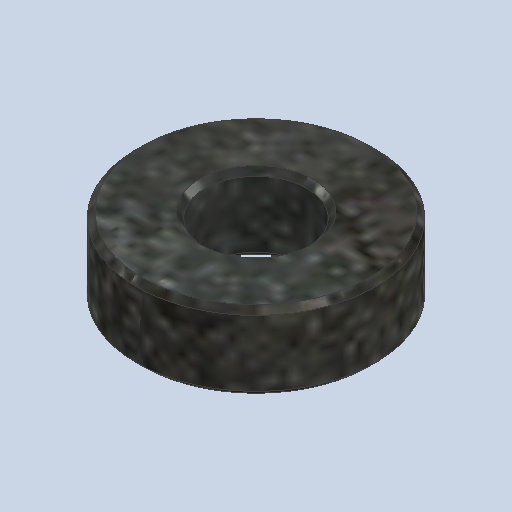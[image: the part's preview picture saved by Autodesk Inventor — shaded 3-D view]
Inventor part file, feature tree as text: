
AUTODESK INVENTOR PART (.ipt)
format: ipt  version: 2024 (Build 280153000, 153)  size: 209,408 bytes
history: native  units: in
note: dims shown in document units (in); Inventor stores cm internally (conversion verified against a paired STEP export)
features: chamfer x1
ambient origin geometry x8: Origin, YZ Plane, XZ Plane, XY Plane, X Axis, Y Axis, Z Axis, Center Point
bodies: Solid1 (feature_tree)
feature tree (1):
  chamfer  "Chamfer1"  [1 undecoded]
note: 1 required parameter value undecoded (feature->parameter linkage not recoverable at this tier; creation-order binding heuristic only, values carry confidence <= 0.55)
